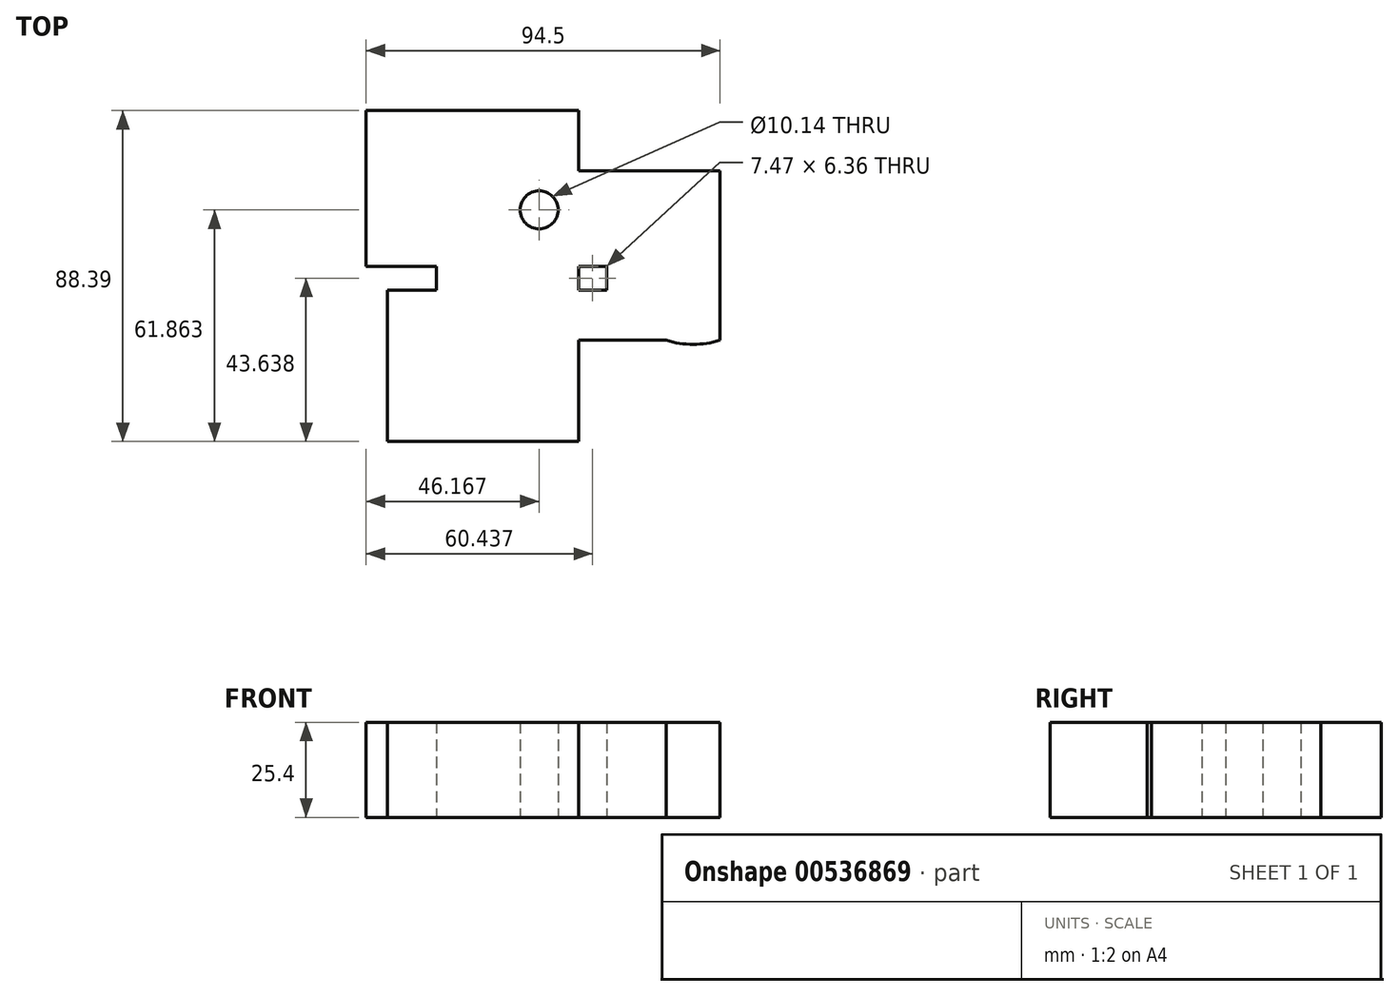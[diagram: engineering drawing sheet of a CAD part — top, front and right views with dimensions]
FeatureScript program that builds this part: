
annotation { "Feature Type Name" : "Feature", "Feature Type Description" : "" }
export const myFeature = defineFeature(function(context is Context, id is Id, definition is map)
    precondition{}
    {
        {
            var Q0;
            Q0=qCreatedBy(makeId("Top.planeOp"),FACE);
            var sketch = newSketch(context, id + "F0", { "sketchPlane" : qUnion([Q0])});
            skLineSegment(sketch, "E0.bottom", {"start": v(-64.17, 47.93) * mm, "end": v(-7.47, 47.93) * mm});
            skLineSegment(sketch, "E0.top", {"start": v(-64.17, 6.36) * mm, "end": v(-7.47, 6.36) * mm});
            skLineSegment(sketch, "E0.left", {"start": v(-64.17, 47.93) * mm, "end": v(-64.17, 6.36) * mm});
            skLineSegment(sketch, "E0.right", {"start": v(-7.47, 47.93) * mm, "end": v(-7.47, 6.36) * mm});
            skLineSegment(sketch, "E1.bottom", {"start": v(-7.47, 6.36) * mm, "end": v(0, 6.36) * mm});
            skLineSegment(sketch, "E1.top", {"start": v(-7.47, 0) * mm, "end": v(0, 0) * mm});
            skLineSegment(sketch, "E1.left", {"start": v(-7.47, 6.36) * mm, "end": v(-7.47, 0) * mm});
            skLineSegment(sketch, "E1.right", {"start": v(0, 6.36) * mm, "end": v(0, 0) * mm});
            skLineSegment(sketch, "E2.bottom", {"start": v(-7.47, 0) * mm, "end": v(-58.52, 0) * mm});
            skLineSegment(sketch, "E2.top", {"start": v(-7.47, -40.46) * mm, "end": v(-58.52, -40.46) * mm});
            skLineSegment(sketch, "E2.left", {"start": v(-7.47, 0) * mm, "end": v(-7.47, -40.46) * mm});
            skLineSegment(sketch, "E2.right", {"start": v(-58.52, 0) * mm, "end": v(-58.52, -40.46) * mm});
            skLineSegment(sketch, "E3.bottom", {"start": v(-45.4, 31.78) * mm, "end": v(30.33, 31.78) * mm});
            skLineSegment(sketch, "E3.top", {"start": v(-45.4, -13.42) * mm, "end": v(30.33, -13.42) * mm});
            skLineSegment(sketch, "E3.left", {"start": v(-45.4, 31.78) * mm, "end": v(-45.4, -13.42) * mm});
            skLineSegment(sketch, "E3.right", {"start": v(30.33, 31.78) * mm, "end": v(30.33, -13.42) * mm});
            skArc(sketch, "E4", {"start": v(30.33, 32.1) * mm, "mid": v(-0.73, 9.34) * mm, "end": v(30.33, -13.42) * mm});
            skLineSegment(sketch, "E5.1", {"start": v(22.73, 10.65) * mm, "end": v(27.15, 3) * mm});
            skLineSegment(sketch, "E5.2", {"start": v(27.15, 3) * mm, "end": v(22.73, -4.66) * mm});
            skLineSegment(sketch, "E5.3", {"start": v(22.73, -4.66) * mm, "end": v(13.89, -4.66) * mm});
            skLineSegment(sketch, "E5.4", {"start": v(13.89, -4.66) * mm, "end": v(11.68, -0.83) * mm});
            skPoint(sketch, "E5.0.midPoint", {"position": v(18.3, 10.65) * mm});
            skArc(sketch, "E6.trimOffspring", {"start": v(11.68, -0.83) * mm, "mid": v(22.14, -3.63) * mm, "end": v(24.94, 6.82) * mm, "construction": true});
            skPoint(sketch, "E5.5.end.orphan", {"position": v(13.89, 10.65) * mm});
            skCircle(sketch, "E7", {"center": v(-18, 21.4) * mm, "radius": 5.07 * mm});
            skSolve(sketch);
        }
        {
            var Q0;
            Q0 = qSketchRegion(id + "F0", true);
            extrude(context, id + "F1", {"entities" : qUnion([Q0]), "depth" : 25.4 * mm, "offsetDistance" : 25.4 * mm});
        }
        {
            var Q0;
            Q0 = qSketchRegion(id + "F0", true);
            extrude(context, id + "F2", {"entities" : qUnion([Q0]), "operationType" : NewBodyOperationType.ADD, "depth" : 25.4 * mm, "offsetDistance" : 25.4 * mm});
        }
    });
